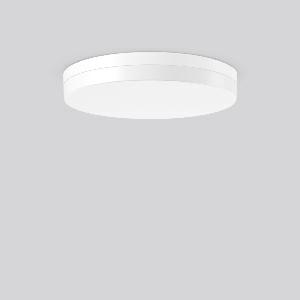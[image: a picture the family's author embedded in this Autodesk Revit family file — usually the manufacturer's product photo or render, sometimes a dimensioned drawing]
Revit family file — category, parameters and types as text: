
# Revit family: flat_slim_round_312633_002_76_3890
name_source: partatom
category: Lighting Fixtures
units: mm (PartAtom-declared; Revit-internal decimal feet)

## family parameters
Cut with Voids When Loaded = No
Host = Face
Light Source = No
Part Type = Normal
Room Calculation Point = No
Round Connector Dimension = Use Diameter
Shared = No

## types (1)
- MultiLumen 1 830 (1 x LED Modul 830, 3350 lm, 3000)
    Apparent Load = 31 VA
    CIE Flux Codes = 41 71 90 86 100
    Color Rendering = 80
    Color Temperature = 3000
    Default Elevation = 1800 mm
    Height = 75 mm
    Lamp = 1 x LED Modul 830
    Lamp Light Flux = 3350 lm
    Lamp count = 1
    Length = 480 mm
    Lifetime = 50000 h
    Luminous efficacy = 108 lm/W
    Manufacturer = RZB
    ModVariant = No
    Model = 312633.002.76
    Mounting Place = Ceiling
    Mounting Type = Surface mounted
    Number of Poles = 1
    OnlyDefault = Yes
    Power Factor = 1
    Product Name = FLAT SLIM round
    Product group = Surface mounted ceiling and wall luminaires
    ProductGroupID = 305
    Protection Class = Protection class I
    Protection Degree = Degree of protection
    RLX_Detail_Level = 1
    RLX_Emergency_Light_Flux = 0 lm
    RLX_Emergency_Type = 0
    RLX_Emergency_Type_DB = No
    RlxData = <blob elided: 21057 chars, md5=fc5119b2>
    Socket = socket
    Standby Power = 0 W
    System Light Flux = 3350 lm
    System Power = 31 W
    Type Comments = MultiLumen 1 830
    Type Image = 312633.002.jpg
    URL = http://relux.com
    VarID = multilumen_1_830
    Voltage = 0 V
    Weight = 0.00 kg
    Width = 0 mm  [stored 0 ft]

note: [stored X ft] marks values corroborated as IEEE doubles in the binary element streams (Revit-internal decimal feet)

## geometry (parser evidence)
native form markers: Blend x4, Sweep x14
no freeform markers — native parametric forms only
